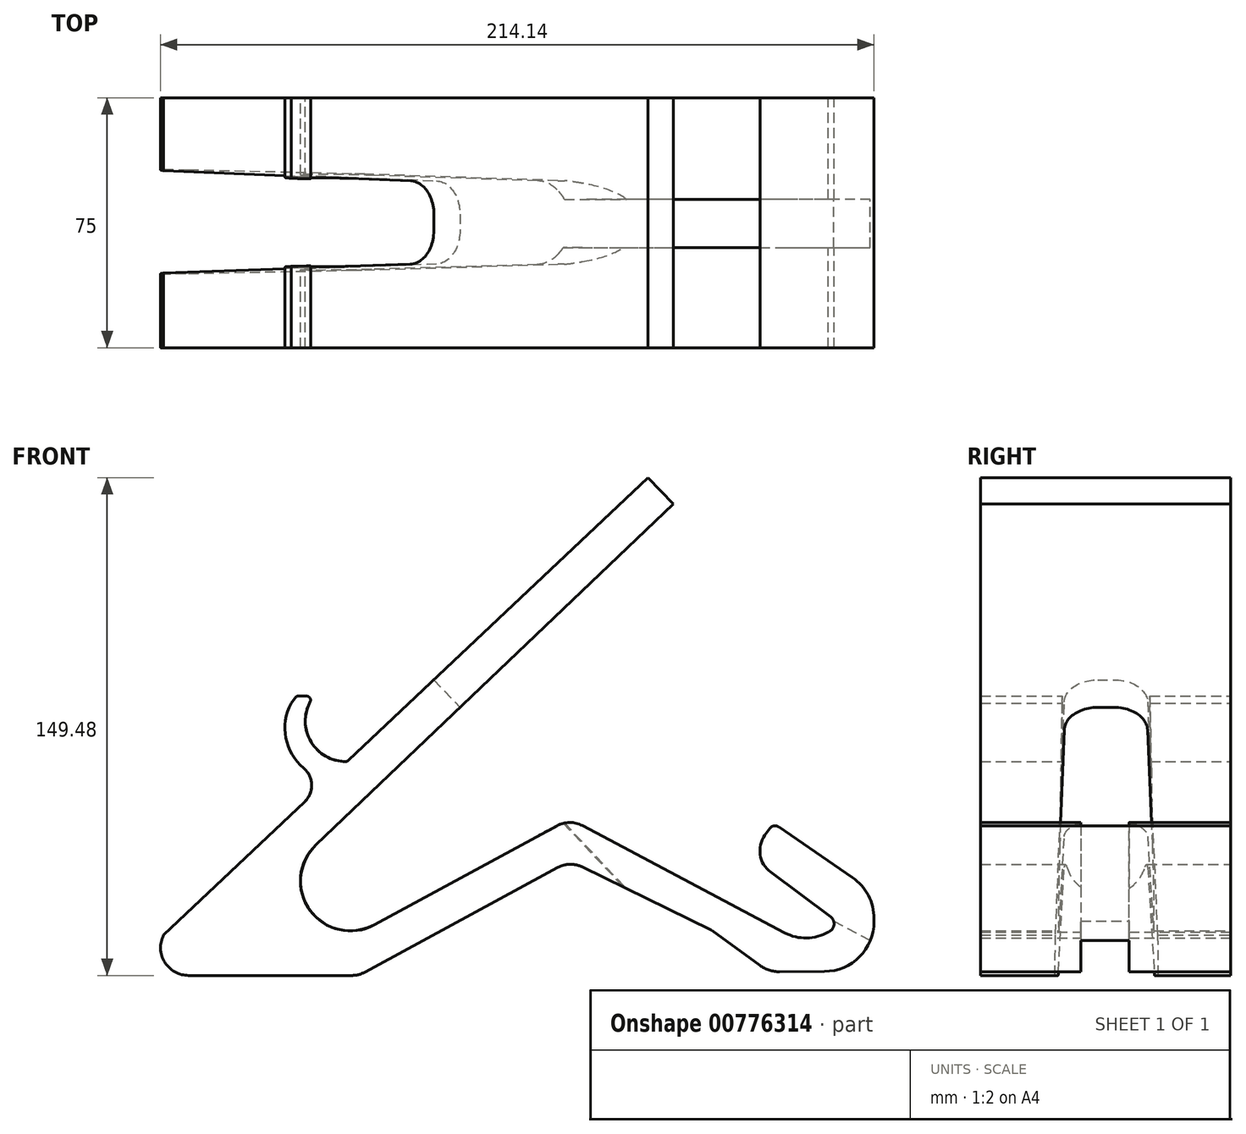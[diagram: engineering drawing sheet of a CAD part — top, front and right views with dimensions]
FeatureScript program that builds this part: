
annotation { "Feature Type Name" : "Feature", "Feature Type Description" : "" }
export const myFeature = defineFeature(function(context is Context, id is Id, definition is map)
    precondition{}
    {
        {
            var Q0;
            Q0=qCreatedBy(makeId("Front.planeOp"),FACE);
            var sketch = newSketch(context, id + "F0", { "sketchPlane" : qUnion([Q0])});
            skLineSegment(sketch, "E0", {"start": v(-54.21, -6.62) * mm, "end": v(35.7, 78.3) * mm});
            skArc(sketch, "E1", {"start": v(-109.68, -59) * mm, "mid": v(-109.36, -67.2) * mm, "end": v(-102.19, -71.18) * mm});
            skPoint(sketch, "E2", {"position": v(-109.68, -59) * mm});
            skArc(sketch, "E3", {"start": v(-71.43, 10.55) * mm, "mid": v(-72.98, 0.14) * mm, "end": v(-67.65, -8.93) * mm});
            skPoint(sketch, "E4", {"position": v(-51.79, -4.33) * mm});
            skArc(sketch, "E5", {"start": v(-65.72, 10.9) * mm, "mid": v(-65.45, -1.06) * mm, "end": v(-55.04, -6.95) * mm});
            skLineSegment(sketch, "E6", {"start": v(-66.8, 12.69) * mm, "end": v(-69.4, 12.69) * mm});
            skLineSegment(sketch, "E7", {"start": v(-69.93, 12.43) * mm, "end": v(-71.43, 10.55) * mm});
            skPoint(sketch, "E8", {"position": v(-54.55, -6.94) * mm});
            skArc(sketch, "E9.filletArc", {"start": v(-65.72, 10.9) * mm, "mid": v(-65.75, 12.1) * mm, "end": v(-66.8, 12.69) * mm});
            skArc(sketch, "E10.filletArc", {"start": v(-69.4, 12.69) * mm, "mid": v(-69.7, 12.62) * mm, "end": v(-69.93, 12.43) * mm});
            skArc(sketch, "E11.filletArc", {"start": v(-55.04, -6.95) * mm, "mid": v(-54.6, -6.86) * mm, "end": v(-54.21, -6.62) * mm});
            skLineSegment(sketch, "E12", {"start": v(43.28, 70.37) * mm, "end": v(-64, -31.97) * mm});
            skLineSegment(sketch, "E13", {"start": v(-67.36, -19.03) * mm, "end": v(-109.68, -59) * mm});
            skLineSegment(sketch, "E14", {"start": v(-46.48, -56) * mm, "end": v(8.37, -26.24) * mm});
            skLineSegment(sketch, "E15", {"start": v(16, -38.62) * mm, "end": v(54.56, -57.5) * mm});
            skLineSegment(sketch, "E16", {"start": v(54.85, -57.67) * mm, "end": v(69.28, -68.15) * mm});
            skArc(sketch, "E17.filletArc", {"start": v(-64, -31.97) * mm, "mid": v(-65.76, -51.65) * mm, "end": v(-46.48, -56) * mm});
            skPoint(sketch, "E18.visualSharp", {"position": v(103.33, -47.38) * mm});
            skArc(sketch, "E19.filletArc", {"start": v(-67.36, -19.03) * mm, "mid": v(-65.24, -13.92) * mm, "end": v(-67.65, -8.93) * mm});
            skLineSegment(sketch, "E20", {"start": v(78.65, -70.03) * mm, "end": v(88.64, -69.97) * mm});
            skLineSegment(sketch, "E21", {"start": v(103.54, -54.97) * mm, "end": v(103.54, -54.12) * mm});
            skLineSegment(sketch, "E22", {"start": v(97.04, -41.76) * mm, "end": v(74.95, -26.57) * mm});
            skArc(sketch, "E23.filletArc", {"start": v(69.28, -68.15) * mm, "mid": v(72.1, -69.58) * mm, "end": v(75.22, -70.05) * mm});
            skArc(sketch, "E24.filletArc", {"start": v(88.64, -69.97) * mm, "mid": v(99.18, -65.54) * mm, "end": v(103.54, -54.97) * mm});
            skPoint(sketch, "E25.visualSharp", {"position": v(103.54, -46.23) * mm});
            skArc(sketch, "E25.filletArc", {"start": v(103.54, -54.12) * mm, "mid": v(101.82, -47.14) * mm, "end": v(97.04, -41.76) * mm});
            skLineSegment(sketch, "E26", {"start": v(75.22, -70.05) * mm, "end": v(78.65, -70.03) * mm});
            skLineSegment(sketch, "E27", {"start": v(-102.19, -71.18) * mm, "end": v(-53.17, -71.18) * mm});
            skLineSegment(sketch, "E28", {"start": v(-49.32, -70.2) * mm, "end": v(8.6, -38.78) * mm});
            skPoint(sketch, "E29.visualSharp", {"position": v(-51.12, -71.18) * mm});
            skArc(sketch, "E29.filletArc", {"start": v(-53.17, -71.18) * mm, "mid": v(-51.18, -70.93) * mm, "end": v(-49.32, -70.2) * mm});
            skLineSegment(sketch, "E30", {"start": v(16, -26.2) * mm, "end": v(76.76, -58.38) * mm});
            skArc(sketch, "E31.filletArc", {"start": v(16, -38.62) * mm, "mid": v(12.29, -37.8) * mm, "end": v(8.6, -38.78) * mm});
            skArc(sketch, "E32.filletArc", {"start": v(16, -26.2) * mm, "mid": v(12.18, -25.27) * mm, "end": v(8.37, -26.24) * mm});
            skLineSegment(sketch, "E33", {"start": v(90.49, -53.56) * mm, "end": v(72.5, -40.17) * mm});
            skLineSegment(sketch, "E34", {"start": v(70.79, -29.07) * mm, "end": v(72.26, -27.04) * mm});
            skPoint(sketch, "E35.visualSharp", {"position": v(66.18, -35.46) * mm});
            skArc(sketch, "E35.filletArc", {"start": v(70.79, -29.07) * mm, "mid": v(69.37, -34.97) * mm, "end": v(72.5, -40.17) * mm});
            skPoint(sketch, "E36.visualSharp", {"position": v(73.37, -25.49) * mm});
            skArc(sketch, "E36.filletArc", {"start": v(74.95, -26.57) * mm, "mid": v(73.5, -26.25) * mm, "end": v(72.26, -27.04) * mm});
            skPoint(sketch, "E37.visualSharp", {"position": v(94.35, -56.44) * mm});
            skArc(sketch, "E37.filletArc", {"start": v(89.78, -58.12) * mm, "mid": v(91.51, -56.05) * mm, "end": v(90.49, -53.56) * mm});
            skPoint(sketch, "E38.visualSharp", {"position": v(77.3, -58.67) * mm});
            skArc(sketch, "E38.filletArc", {"start": v(76.76, -58.38) * mm, "mid": v(83.3, -59.94) * mm, "end": v(89.78, -58.12) * mm});
            skPoint(sketch, "E39.visualSharp", {"position": v(54.7, -57.57) * mm});
            skArc(sketch, "E39.filletArc", {"start": v(54.85, -57.67) * mm, "mid": v(54.7, -57.58) * mm, "end": v(54.56, -57.5) * mm});
            skLineSegment(sketch, "E40", {"start": v(43.28, 70.37) * mm, "end": v(35.7, 78.3) * mm});
            skSolve(sketch);
        }
        {
            var Q0;
            Q0=makeQuery(id+"F0.imprint","IMPRINT",FACE,{"disambiguationData":[TD([[makeQuery(id+"F0.imprint","IMPRINT",EDGE,{"derivedFrom":sQuery(id+"F0.wireOp",EDGE,"E0")}),-1.0]])]});
            extrude(context, id + "F1", {"entities" : qUnion([Q0]), "depth" : 75 * mm, "offsetDistance" : 25 * mm});
        }
        {
            var Q0;
            Q0=makeQuery(id+"F1.opExtrude","SWEPT_FACE",FACE,{"disambiguationData":[OSD([sQuery(id+"F0.wireOp",EDGE,"E0")])]});
            var sketch = newSketch(context, id + "F2", { "sketchPlane" : qUnion([Q0])});
            skLineSegment(sketch, "E41", {"start": v(-144, -21.08) * mm, "end": v(-18.39, -24.91) * mm});
            skLineSegment(sketch, "E42", {"start": v(-8.7, -34.9) * mm, "end": v(-8.7, -39.9) * mm});
            skLineSegment(sketch, "E43", {"start": v(-18.43, -49.9) * mm, "end": v(-143.46, -53.26) * mm});
            skLineSegment(sketch, "E44", {"start": v(-143.46, -53.26) * mm, "end": v(-144, -21.08) * mm});
            skPoint(sketch, "E45.visualSharp", {"position": v(-8.7, -25.2) * mm});
            skArc(sketch, "E45.filletArc", {"start": v(-8.7, -34.9) * mm, "mid": v(-11.52, -27.94) * mm, "end": v(-18.39, -24.91) * mm});
            skPoint(sketch, "E46.visualSharp", {"position": v(-8.7, -49.64) * mm});
            skArc(sketch, "E46.filletArc", {"start": v(-18.43, -49.9) * mm, "mid": v(-11.53, -46.88) * mm, "end": v(-8.7, -39.9) * mm});
            skSolve(sketch);
        }
        {
            var Q0;
            {var subQ0=sQuery(id+"F2.wireOp",EDGE,"E44");Q0=makeQuery(id+"F2.imprint","IMPRINT",FACE,{"disambiguationData":[TD([[makeQuery(id+"F2.imprint","IMPRINT",EDGE,{"derivedFrom":subQ0}),-1.0]])]});}
            var Q1;
            Q1=makeQuery(id+"F2.imprint","IMPRINT",FACE,{"disambiguationData":[TD([[makeQuery(id+"F2.imprint","IMPRINT",EDGE,{"derivedFrom":sQuery(id+"F2.wireOp",EDGE,"E42")}),-1.0]])]});
            extrude(context, id + "F3", {"entities" : qUnion([Q0, Q1]), "operationType" : NewBodyOperationType.REMOVE, "depth" : 30 * mm, "offsetDistance" : 25 * mm, "hasSecondDirection" : true, "secondDirectionOppositeDirection" : true, "secondDirectionDepth" : 90 * mm});
        }
        {
            var Q0;
            Q0=makeQuery(id+"F1.opExtrude","SWEPT_FACE",FACE,{"disambiguationData":[OSD([sQuery(id+"F0.wireOp",EDGE,"E30")])]});
            var sketch = newSketch(context, id + "F4", { "sketchPlane" : qUnion([Q0])});
            skLineSegment(sketch, "E47", {"start": v(16.24, -44.93) * mm, "end": v(131.28, -44.93) * mm});
            skLineSegment(sketch, "E48", {"start": v(136.28, -39.93) * mm, "end": v(136.28, -35.46) * mm});
            skLineSegment(sketch, "E49", {"start": v(131.28, -30.46) * mm, "end": v(16.24, -30.46) * mm});
            skLineSegment(sketch, "E50", {"start": v(11.24, -35.46) * mm, "end": v(11.24, -39.93) * mm});
            skPoint(sketch, "E51.visualSharp", {"position": v(11.24, -44.93) * mm});
            skArc(sketch, "E51.filletArc", {"start": v(11.24, -39.93) * mm, "mid": v(12.7, -43.47) * mm, "end": v(16.24, -44.93) * mm});
            skPoint(sketch, "E52.visualSharp", {"position": v(11.24, -30.46) * mm});
            skArc(sketch, "E52.filletArc", {"start": v(16.24, -30.46) * mm, "mid": v(12.7, -31.92) * mm, "end": v(11.24, -35.46) * mm});
            skPoint(sketch, "E53.visualSharp", {"position": v(136.28, -44.93) * mm});
            skArc(sketch, "E53.filletArc", {"start": v(131.28, -44.93) * mm, "mid": v(134.82, -43.47) * mm, "end": v(136.28, -39.93) * mm});
            skPoint(sketch, "E54.visualSharp", {"position": v(136.28, -30.46) * mm});
            skArc(sketch, "E54.filletArc", {"start": v(136.28, -35.46) * mm, "mid": v(134.82, -31.92) * mm, "end": v(131.28, -30.46) * mm});
            skSolve(sketch);
        }
        {
            var Q0;
            {var subQ0=sQuery(id+"F4.wireOp",EDGE,"E47");var subQ1=sQuery(id+"F0.wireOp",EDGE,"E30");var subQ2=makeQuery(id+"F1.opExtrude","SWEPT_EDGE",EDGE,{"disambiguationData":[OSD([subQ1,sQuery(id+"F0.wireOp",EDGE,"E32.filletArc")])]});var subQ3=makeQuery(id+"F4.imprint","INTERSECT",VERTEX,{"derivedFrom":[subQ2,subQ0]});Q0=makeQuery(id+"F4.imprint","IMPRINT",FACE,{"disambiguationData":[TD([[makeQuery(id+"F4.imprint","IMPRINT",EDGE,{"disambiguationData":[TD([[subQ3,-1.0]])],"derivedFrom":subQ0}),1.0]])]});}
            var Q1;
            Q1=makeQuery(id+"F4.imprint","IMPRINT",FACE,{"disambiguationData":[TD([[makeQuery(id+"F4.imprint","IMPRINT",EDGE,{"derivedFrom":sQuery(id+"F4.wireOp",EDGE,"E50")}),1.0]])]});
            var Q2;
            Q2=makeQuery(id+"F4.imprint","IMPRINT",FACE,{"disambiguationData":[TD([[makeQuery(id+"F4.imprint","IMPRINT",EDGE,{"derivedFrom":sQuery(id+"F4.wireOp",EDGE,"E48")}),1.0]])]});
            extrude(context, id + "F5", {"entities" : qUnion([Q0, Q1, Q2]), "operationType" : NewBodyOperationType.REMOVE, "oppositeDirection" : true, "depth" : 25 * mm, "offsetDistance" : 25 * mm, "hasSecondDirection" : true, "secondDirectionOppositeDirection" : false, "secondDirectionDepth" : 10 * mm});
        }
    });
